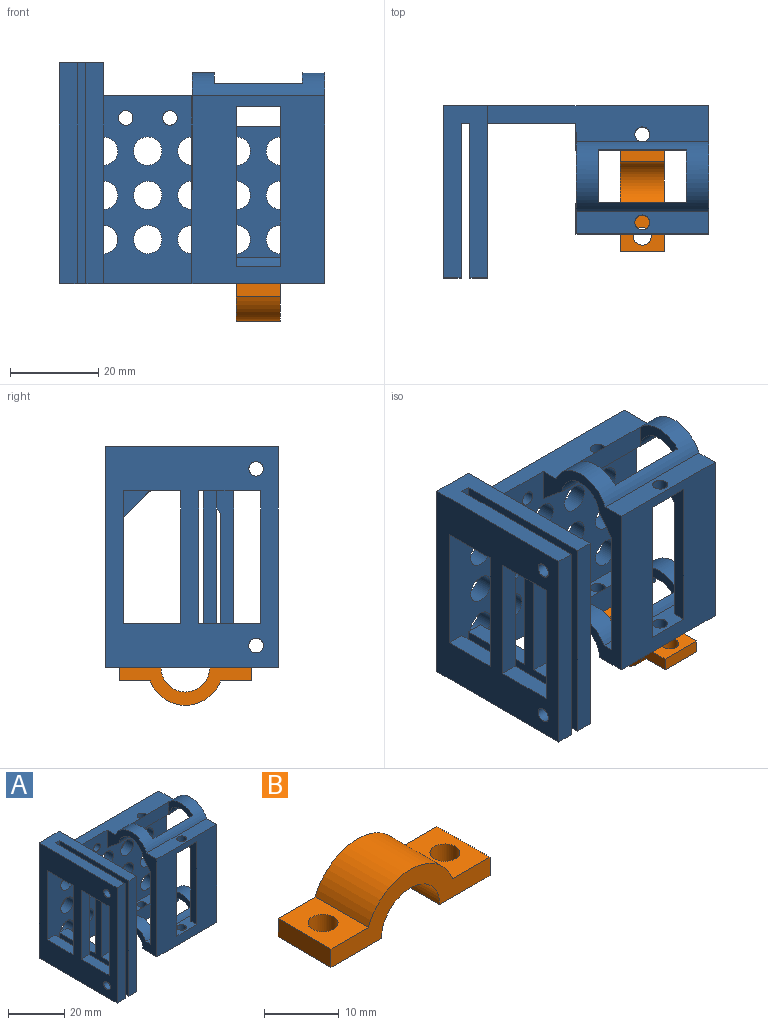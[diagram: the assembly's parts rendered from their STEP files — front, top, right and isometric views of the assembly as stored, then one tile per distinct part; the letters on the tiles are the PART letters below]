
ASSEMBLY  parts=2 mates=1
PART A: 90 faces, bbox 60x39x50 mm
  f0: plane 60x50mm, normal (0,-1,0), area 1609.4mm2, adj f2,f4,f15,f16,f20,f23,f24,f26
  f1: plane 60x50mm, normal (0,1,0), area 2075.3mm2, adj f2,f16,f23,f24,f26,f50,f51,f53
  f2: plane 60x39mm, normal (0,0,-1), area 574.9mm2, adj f0,f1,f6,f15,f23,f24,f26,f28
  f3: plane 10x5mm, normal (0,0.78,-0.63), area 63.9mm2, adj f5,f10,f13,f26,f79,f80
  f4: plane 10x6.05mm, normal (0,-0.64,-0.77), area 78.2mm2, adj f0,f5,f26,f50,f79,f82
  f5: cylinder r=6mm len=11.9mm, axis (1,0,0), area 86.6mm2, adj f3,f4,f26,f79
  f6: cylinder r=6mm len=12mm, axis (1,0,0), area 94.2mm2, adj f2,f25,f26,f78
  f7: plane 10x5mm, normal (0,0.78,-0.63), area 63.9mm2, adj f9,f15,f17,f47,f80,f81
  f8: plane 10x7mm, normal (0,0,-1), area 60.9mm2, adj f9,f10,f14,f80,f84
  f9: plane 36x7mm, normal (1,0,0), area 118.1mm2, adj f7,f8,f14,f17,f56,f80
  f10: plane 36x7mm, normal (-1,0,0), area 118.1mm2, adj f3,f8,f13,f14,f56,f80
  f11: cylinder r=8.5mm len=30mm, axis (1,0,0), area 333.6mm2, adj f15,f26,f53,f54,f79,f80,f81,f82
  f12: cylinder r=8.5mm len=30mm, axis (1,0,0), area 284.8mm2, adj f15,f26,f55,f56,f75,f76,f77,f78
  f13: plane 31x10mm, normal (0,1,0), area 310mm2, adj f3,f10,f26,f56
  f14: plane 42.5x30mm, normal (0,-1,0), area 915mm2, adj f8,f9,f10,f15,f25,f26,f54,f56
  f15: plane 47.74x25mm, normal (-1,0,0), area 299.3mm2, adj f0,f2,f7,f11,f12,f14,f17,f25
  f16: plane 39x10mm, normal (0,0,1), area 320mm2, adj f0,f1,f23,f24,f28,f30,f32,f33
  f17: plane 31x10mm, normal (0,1,0), area 310mm2, adj f7,f9,f15,f56
  f18: plane 14x4mm, normal (0,0,1), area 56mm2, adj f24,f28,f41,f46
  f19: plane 14x4mm, normal (0,0,-1), area 56mm2, adj f24,f28,f41,f46
  f20: plane 18x4mm, normal (0,0,1), area 72mm2, adj f0,f23,f30,f42,f61
  f21: plane 10x4mm, normal (0,0,-1), area 40mm2, adj f23,f30,f40,f43
  f22: plane 17x4mm, normal (0,0,-1), area 68mm2, adj f23,f30,f31,f32
  f23: plane 50x39mm, normal (1,0,0), area 827.8mm2, adj f0,f1,f2,f16,f20,f21,f22,f29
  f24: plane 50x39mm, normal (-1,0,0), area 1122.9mm2, adj f0,f1,f2,f16,f18,f19,f27,f33
  f25: plane 30x7mm, normal (0,0,-1), area 200.9mm2, adj f6,f14,f15,f26,f48,f77,f83
  f26: plane 47.74x29mm, normal (1,0,0), area 469.3mm2, adj f0,f1,f2,f3,f4,f5,f6,f11
  f27: plane 13x4mm, normal (0,0,1), area 52mm2, adj f0,f24,f28,f45
  f28: plane 50x35mm, normal (1,0,0), area 922.9mm2, adj f0,f2,f16,f18,f19,f27,f33,f35
  f29: plane 10x4mm, normal (0,0,1), area 40mm2, adj f23,f30,f40,f43
  f30: plane 50x35mm, normal (-1,0,0), area 797.8mm2, adj f0,f2,f16,f20,f21,f22,f29,f31
  f31: cylinder r=6mm len=12mm, axis (1,0,0), area 75.4mm2, adj f2,f22,f23,f30
  f32: plane 50x4mm, normal (0,-1,0), area 200mm2, adj f16,f22,f23,f30
  f33: plane 50x4mm, normal (0,-1,0), area 200mm2, adj f2,f16,f24,f28
  f34: cylinder r=1.65mm len=4mm, axis (1,0,0), area 41.5mm2, adj f23,f30
  f35: cylinder r=1.65mm len=4mm, axis (1,0,0), area 41.5mm2, adj f24,f28
  f36: plane 13x4mm, normal (0,0,-1), area 52mm2, adj f0,f24,f28,f45
  f37: cylinder r=6mm len=12mm, axis (1,0,0), area 75.4mm2, adj f23,f30,f42,f44
  f38: cylinder r=1.65mm len=4mm, axis (-1,0,0), area 41.5mm2, adj f23,f30
  f39: cylinder r=1.65mm len=4mm, axis (-1,0,0), area 41.5mm2, adj f24,f28
  f40: plane 30x4mm, normal (0,1,0), area 120mm2, adj f21,f23,f29,f30
  f41: plane 30x4mm, normal (0,1,0), area 120mm2, adj f18,f19,f24,f28
  f42: plane 30x4mm, normal (0,1,0), area 120mm2, adj f20,f23,f30,f37
  f43: plane 30x4mm, normal (0,-1,0), area 120mm2, adj f21,f23,f29,f30
  f44: plane 6x6mm, normal (0,-0.71,-0.71), area 33.9mm2, adj f0,f23,f30,f37
  f45: plane 30x4mm, normal (0,1,0), area 120mm2, adj f24,f27,f28,f36
  f46: plane 30x4mm, normal (0,-1,0), area 120mm2, adj f18,f19,f24,f28
  f47: cylinder r=6mm len=11.9mm, axis (1,0,0), area 86.6mm2, adj f7,f15,f49,f81
  f48: cylinder r=6mm len=12mm, axis (1,0,0), area 94.2mm2, adj f2,f15,f25,f76
  f49: plane 10x6.05mm, normal (0,-0.64,-0.77), area 78.2mm2, adj f0,f15,f47,f51,f81,f82
  f50: plane 10x5.5mm, normal (-1,0,0), area 35.1mm2, adj f0,f1,f4,f52,f82,f87,f88,f89
  f51: plane 10x5.5mm, normal (1,0,0), area 35.1mm2, adj f0,f1,f49,f52,f82,f87,f88,f89
  f52: plane 10x6mm, normal (0,0,-1), area 50.9mm2, adj f50,f51,f82,f86,f87
  f53: plane 50x8.15mm, normal (0,0,1), area 315.5mm2, adj f0,f1,f11,f15,f23,f26,f86
  f54: plane 30x5.15mm, normal (0,0,1), area 145.5mm2, adj f11,f14,f15,f26,f84
  f55: plane 30x4.5mm, normal (0,0,1), area 125.9mm2, adj f0,f12,f15,f26,f85
  f56: plane 30x5.5mm, normal (0,0,1), area 95.9mm2, adj f9,f10,f12,f13,f14,f15,f17,f26
  f57: cylinder r=3.2mm len=6.4mm, axis (0,1,0), area 80.4mm2, adj f0,f1
  f58: cylinder r=1.65mm len=4mm, axis (0,1,0), area 41.5mm2, adj f0,f1
  f59: cylinder r=3.2mm len=6.4mm, axis (0,1,0), area 80.4mm2, adj f0,f1
  f60: cylinder r=3.2mm len=6.4mm, axis (0,1,0), area 80.4mm2, adj f0,f1
  f61: plane 3.2x3.2mm, normal (0,1,0), area 8mm2, adj f20,f23,f62
  f62: cylinder r=3.2mm len=6.4mm, axis (0,1,0), area 80.4mm2, adj f0,f1,f61
  f63: cylinder r=3.2mm len=6.4mm, axis (0,1,0), area 80.4mm2, adj f0,f1
  f64: cylinder r=3.2mm len=6.4mm, axis (0,1,0), area 80.4mm2, adj f0,f1
  f65: cylinder r=3.2mm len=6.4mm, axis (0,1,0), area 80.4mm2, adj f0,f1
  f66: cylinder r=3.2mm len=6.4mm, axis (0,1,0), area 80.4mm2, adj f0,f1
  f67: cylinder r=3.2mm len=6.4mm, axis (0,1,0), area 80.4mm2, adj f0,f1
  f68: cylinder r=1.65mm len=4mm, axis (0,1,0), area 41.5mm2, adj f0,f1
  f69: cylinder r=3.2mm len=6.4mm, axis (0,1,0), area 80.4mm2, adj f0,f1
  f70: cylinder r=3.2mm len=6.4mm, axis (0,1,0), area 80.4mm2, adj f0,f1
  f71: cylinder r=3.2mm len=6.4mm, axis (0,1,0), area 80.4mm2, adj f0,f1
  f72: cylinder r=3.2mm len=6.4mm, axis (0,1,0), area 80.4mm2, adj f0,f1
  f73: cylinder r=3.2mm len=6.4mm, axis (0,1,0), area 80.4mm2, adj f0,f1
  f74: cylinder r=3.2mm len=6.4mm, axis (0,1,0), area 80.4mm2, adj f0,f1
  f75: plane 20x6.02mm, normal (0,-1,0), area 120.4mm2, adj f2,f12,f76,f78
  f76: plane 12x8.5mm, normal (1,0,0), area 36.2mm2, adj f12,f48,f75,f77
  f77: plane 20x6.02mm, normal (0,1,0), area 120.4mm2, adj f12,f25,f76,f78
  f78: plane 12x8.5mm, normal (-1,0,0), area 36.2mm2, adj f6,f12,f75,f77
  f79: plane 12x7.8mm, normal (-1,0,0), area 36.2mm2, adj f3,f4,f5,f11,f80,f82
  f80: plane 20x5.32mm, normal (0,1,0), area 105.7mm2, adj f3,f7,f8,f9,f10,f11,f79,f81
  f81: plane 12x7.8mm, normal (1,0,0), area 36.2mm2, adj f7,f11,f47,f49,f80,f82
  f82: plane 20x5.3mm, normal (0,-1,0), area 105.5mm2, adj f4,f11,f49,f50,f51,f52,f79,f81
  f83: cylinder r=1.7mm len=4mm, axis (0,0,1), area 42.7mm2, adj f25,f56
  f84: cylinder r=1.7mm len=3.4mm, axis (0,0,1), area 26.7mm2, adj f8,f54
  f85: cylinder r=1.7mm len=4mm, axis (0,0,-1), area 42.7mm2, adj f2,f55
  f86: cylinder r=1.7mm len=3.4mm, axis (0,0,-1), area 26.8mm2, adj f11,f52,f53
  f87: plane 10x0.5mm, normal (0,1,0), area 5mm2, adj f50,f51,f52,f88
  f88: plane 10x4mm, normal (0,0,-1), area 40mm2, adj f1,f50,f51,f87
  f89: plane 10x4mm, normal (0,0,1), area 40mm2, adj f0,f1,f50,f51
PART B: 12 faces, bbox 30x10x8.5 mm
  f0: plane 10x3mm, normal (-1,0,0), area 30mm2, adj f3,f4,f5,f6
  f1: plane 10x3mm, normal (1,0,0), area 30mm2, adj f2,f3,f4,f8
  f2: plane 10x9.5mm, normal (0,0,-1), area 82.4mm2, adj f1,f3,f4,f9,f10
  f3: plane 30x8.5mm, normal (0,-1,0), area 106.1mm2, adj f0,f1,f2,f5,f6,f7,f8,f9
  f4: plane 30x8.5mm, normal (0,1,0), area 106.1mm2, adj f0,f1,f2,f5,f6,f7,f8,f9
  f5: plane 10x9.5mm, normal (0,0,-1), area 82.4mm2, adj f0,f3,f4,f9,f11
  f6: plane 10x7.05mm, normal (0,0,1), area 57.9mm2, adj f0,f3,f4,f7,f11
  f7: cylinder r=8.5mm len=15.91mm, axis (0,-1,0), area 205.7mm2, adj f3,f4,f6,f8
  f8: plane 10x7.05mm, normal (0,0,1), area 57.9mm2, adj f1,f3,f4,f7,f10
  f9: cylinder r=5.5mm len=11mm, axis (0,-1,0), area 172.8mm2, adj f2,f3,f4,f5
  f10: cylinder r=2mm len=4mm, axis (0,0,1), area 37.7mm2, adj f2,f8
  f11: cylinder r=2mm len=4mm, axis (0,0,1), area 37.7mm2, adj f5,f6
PLACE A t=(-10.28,11.22,-8.52)mm
PLACE B rot(axis=(0.71,-0.71,0),180deg) t=(6.13,-0.93,-28.52)mm
MATE fastened B.f11 <-> A.f85  axis (0,0,1) through (4.72,4.72,-28.52)mm
